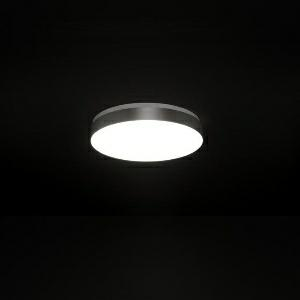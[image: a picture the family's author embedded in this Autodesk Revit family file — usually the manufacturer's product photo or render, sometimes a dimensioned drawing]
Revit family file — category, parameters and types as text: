
# Revit family: spectral_norea_norea-rp_416_4300_840_mps_b4df
name_source: partatom
category: Lighting Fixtures
revit_build: Autodesk Revit 2016 (Build: 20150220_1215(x64)
units: mm (PartAtom-declared; Revit-internal decimal feet)

## family parameters
Cut with Voids When Loaded = No
Host = Face
Light Source = No
Part Type = Normal
Room Calculation Point = No
Round Connector Dimension = Use Diameter
Shared = No

## types (1)
- SPECTRAL NOREA (1 x )
    Apparent Load = 0 VA
    Approval mark = CE
    CIE Flux Codes = 73 93 98 100 62
    Control Gear = Electronic transformer
    Default Elevation = 1800 mm
    Description = SPT0000138
NOREA Pendant luminaire

Design:
Round luminaire element with a microprism panel in a natural anodised aluminium profile frame surround. The frame is fixed at the powder-coated metal body by a bayonet fixture with spring clip. The luminaire is suspended by a six trapezoidal wire pendants with ceiling fixture and transparent connecting cable round ceiling junction box. Cable length adjustable at the junction box, steel wire steplessly height adjustable. The metal body accommodates the electrical components and electronic ballast. The LED module is formed as a round LED flat board and can be removed for mounting or exchange using a keyhole screw connection. Plug-in electrical connection of the LED flat board. Luminaire with heat-resistant wiring. Variant suitable for office use with a microprism panel MPS. The LED points are visible as circles on the microprism panel. Also in a dimmable version.
Protection rating IP20, safety class I.

Colour:
Housing – similar to RAL 9016 White silk matt;
Frame – natural anodised
    Height = 78 mm  [stored 0.255906 ft]
    Lamp = 1 x
    Lamp count = 1
    Length = 416 mm
    Luminous efficacy = 0 lm/W
    Manufacturer = Ridi
    ModVariant = No
    Model = NOREA-RP 416/4300/840 MPS
    Mounting Place = Ceiling
    Mounting Type = Pendant
    Number of Poles = 1
    OnlyDefault = Yes
    Power Factor = 1
    Product Name = SPECTRAL NOREA
    Product group = Pendant luminaire
    ProductGroupID = 9
    Protection Class = Protection class
    Protection Degree = IP 20
    RlxData = <blob elided: 30341 chars, md5=9e37d066>
    Socket = socket
    Standby Power = 0 W
    System Light Flux = 0 lm
    System Power = 0 W
    Type Image = rundmittel01_-_kopie.jpg
    URL = http://reluxnet.relux.com
    VarID = 1
    Voltage = 0 V
    Weight = 0.00 kg
    Width = 0 mm  [stored 0 ft]

note: [stored X ft] marks values corroborated as IEEE doubles in the binary element streams (Revit-internal decimal feet)

## geometry (parser evidence)
native form markers: Sweep x10
no freeform markers — native parametric forms only
